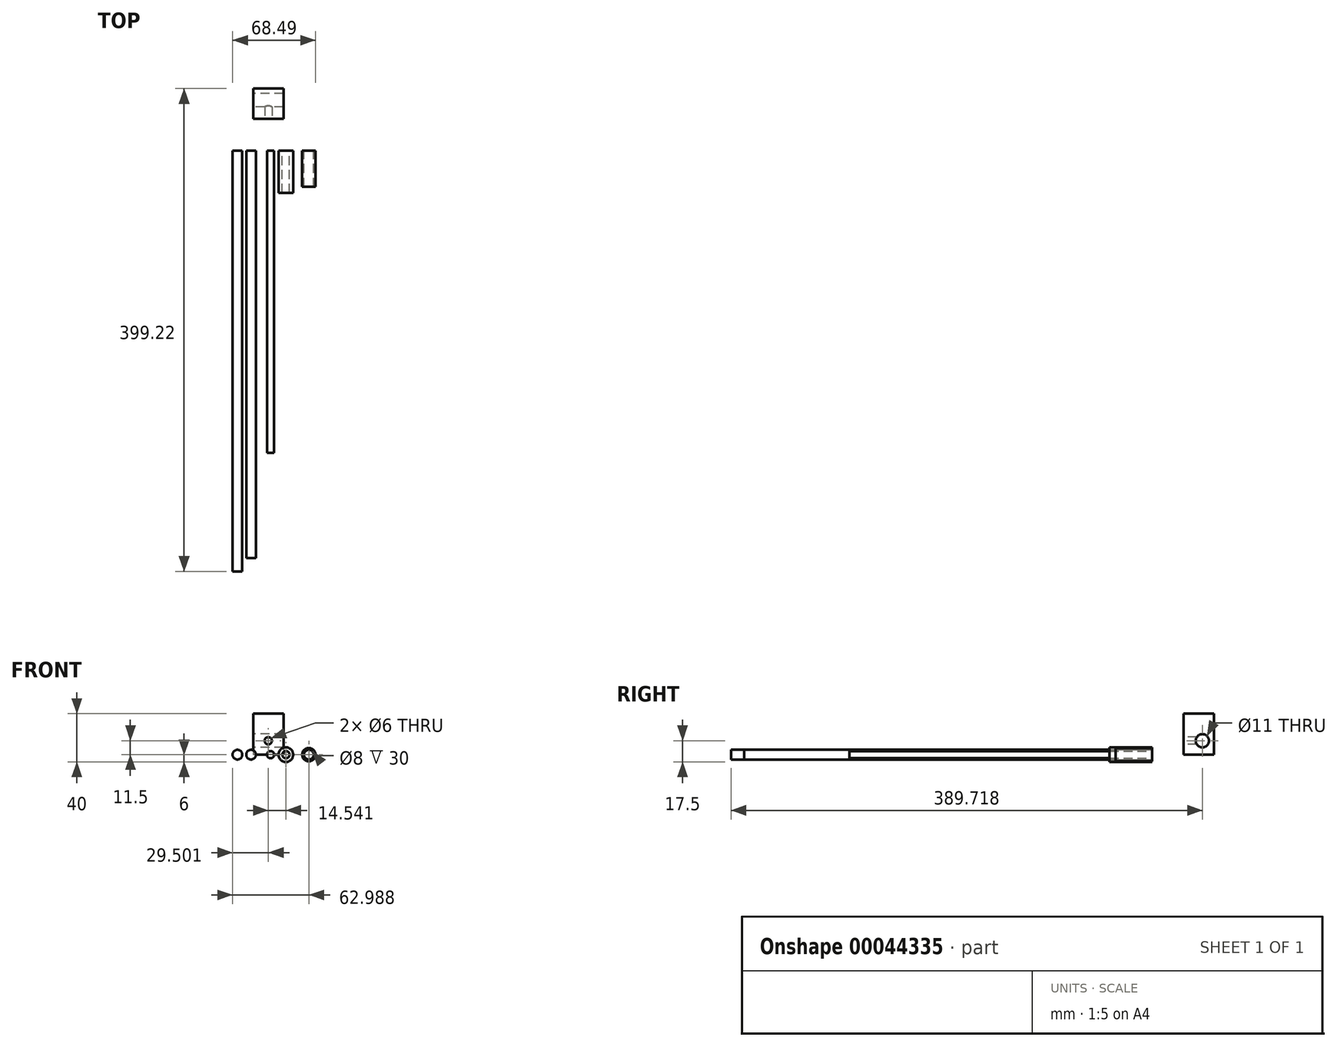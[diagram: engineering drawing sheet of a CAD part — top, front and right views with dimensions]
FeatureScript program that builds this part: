
annotation { "Feature Type Name" : "Feature", "Feature Type Description" : "" }
export const myFeature = defineFeature(function(context is Context, id is Id, definition is map)
    precondition{}
    {
        {
            var Q0;
            Q0=qCreatedBy(makeId("Front.planeOp"),FACE);
            var sketch = newSketch(context, id + "F0", { "sketchPlane" : qUnion([Q0])});
            skCircle(sketch, "E0", {"center": v(-61.9, 0) * mm, "radius": 4 * mm});
            skSolve(sketch);
        }
        {
            var Q0;
            Q0=makeQuery(id+"F0.imprint","IMPRINT",FACE,{"disambiguationData":[TD([[makeQuery(id+"F0.imprint","IMPRINT",EDGE,{"derivedFrom":sQuery(id+"F0.wireOp",EDGE,"E0")}),1.0]])]});
            extrude(context, id + "F1", {"entities" : qUnion([Q0]), "depth" : 348 * mm});
        }
        {
            var Q0;
            Q0=qCreatedBy(makeId("Front.planeOp"),FACE);
            var sketch = newSketch(context, id + "F2", { "sketchPlane" : qUnion([Q0])});
            skCircle(sketch, "E1", {"center": v(-45.77, 0) * mm, "radius": 3 * mm});
            skSolve(sketch);
        }
        {
            var Q0;
            Q0=makeQuery(id+"F2.imprint","IMPRINT",FACE,{"disambiguationData":[TD([[makeQuery(id+"F2.imprint","IMPRINT",EDGE,{"derivedFrom":sQuery(id+"F2.wireOp",EDGE,"E1")}),1.0]])]});
            extrude(context, id + "F3", {"entities" : qUnion([Q0]), "depth" : 250 * mm});
        }
        {
            var Q0;
            Q0=qCreatedBy(makeId("Front.planeOp"),FACE);
            var sketch = newSketch(context, id + "F4", { "sketchPlane" : qUnion([Q0])});
            skCircle(sketch, "E2", {"center": v(-33.08, 0) * mm, "radius": 3 * mm});
            skCircle(sketch, "E3", {"center": v(-33.08, 0) * mm, "radius": 6 * mm});
            skSolve(sketch);
        }
        {
            var Q0;
            Q0=makeQuery(id+"F4.imprint","IMPRINT",FACE,{"disambiguationData":[TD([[makeQuery(id+"F4.imprint","IMPRINT",EDGE,{"derivedFrom":sQuery(id+"F4.wireOp",EDGE,"E2")}),-1.0]])]});
            extrude(context, id + "F5", {"entities" : qUnion([Q0]), "depth" : 35 * mm});
        }
        {
            var Q0;
            Q0=makeQuery(id+"F1.opExtrude","SWEPT_BODY",BODY,{"disambiguationData":[OSD([sQuery(id+"F0.wireOp",EDGE,"E0")])]});
            transform(context, id + "F6", {"entities" : qUnion([Q0]), "transformType" : TransformType.TRANSLATION_3D, "dx" : -11.23 * mm, "dy" : 0 * mm, "dz" : 0 * mm, "makeCopy" : false});
        }
        {
            var Q0;
            Q0=qSketchRegion(id+"F0",true);
            extrude(context, id + "F7", {"entities" : qUnion([Q0]), "depth" : 337 * mm});
        }
        {
            var Q0;
            Q0=qCreatedBy(makeId("Front.planeOp"),FACE);
            var sketch = newSketch(context, id + "F8", { "sketchPlane" : qUnion([Q0])});
            skCircle(sketch, "E4", {"center": v(-14.13, 0) * mm, "radius": 4 * mm});
            skCircle(sketch, "E5", {"center": v(-14.13, 0) * mm, "radius": 5.5 * mm});
            skSolve(sketch);
        }
        {
            var Q0;
            Q0=makeQuery(id+"F8.imprint","IMPRINT",FACE,{"disambiguationData":[TD([[makeQuery(id+"F8.imprint","IMPRINT",EDGE,{"derivedFrom":sQuery(id+"F8.wireOp",EDGE,"E4")}),-1.0]])]});
            extrude(context, id + "F9", {"entities" : qUnion([Q0]), "depth" : 30 * mm});
        }
        {
            var Q0;
            Q0=qCreatedBy(makeId("Top.planeOp"),FACE);
            var sketch = newSketch(context, id + "F10", { "sketchPlane" : qUnion([Q0])});
            skLineSegment(sketch, "E6.bottom", {"start": v(-35.12, 51.22) * mm, "end": v(-60.12, 51.22) * mm});
            skLineSegment(sketch, "E6.top", {"start": v(-35.12, 26.22) * mm, "end": v(-60.12, 26.22) * mm});
            skLineSegment(sketch, "E6.left", {"start": v(-35.12, 51.22) * mm, "end": v(-35.12, 26.22) * mm});
            skLineSegment(sketch, "E6.right", {"start": v(-60.12, 51.22) * mm, "end": v(-60.12, 26.22) * mm});
            skSolve(sketch);
        }
        {
            var Q0;
            Q0=makeQuery(id+"F10.imprint","IMPRINT",FACE,{"disambiguationData":[TD([[makeQuery(id+"F10.imprint","IMPRINT",EDGE,{"derivedFrom":sQuery(id+"F10.wireOp",EDGE,"E6.bottom")}),1.0]])]});
            extrude(context, id + "F11", {"entities" : qUnion([Q0]), "depth" : 34 * mm});
        }
        {
            var Q0;
            Q0=makeQuery(id+"F11.opExtrude","SWEPT_FACE",FACE,{"disambiguationData":[OSD([sQuery(id+"F10.wireOp",EDGE,"E6.right")])]});
            var sketch = newSketch(context, id + "F12", { "sketchPlane" : qUnion([Q0])});
            skLineSegment(sketch, "E7", {"start": v(-32.12, 0) * mm, "end": v(-51.22, 0) * mm, "construction": true});
            skLineSegment(sketch, "E8", {"start": v(-51.22, 0) * mm, "end": v(-51.22, 22.36) * mm, "construction": true});
            skCircle(sketch, "E9", {"center": v(-41.72, 11.5) * mm, "radius": 5.5 * mm});
            skSolve(sketch);
        }
        {
            var Q0;
            Q0=makeQuery(id+"F12.imprint","IMPRINT",FACE,{"disambiguationData":[TD([[makeQuery(id+"F12.imprint","IMPRINT",EDGE,{"derivedFrom":sQuery(id+"F12.wireOp",EDGE,"E9")}),1.0]])]});
            extrude(context, id + "F13", {"entities" : qUnion([Q0]), "operationType" : NewBodyOperationType.REMOVE, "endBound" : BoundingType.THROUGH_ALL, "oppositeDirection" : true, "depth" : 25 * mm});
        }
        {
            var Q0;
            Q0=makeQuery(id+"F11.opExtrude","SWEPT_FACE",FACE,{"disambiguationData":[OSD([sQuery(id+"F10.wireOp",EDGE,"E6.top")])]});
            var sketch = newSketch(context, id + "F14", { "sketchPlane" : qUnion([Q0])});
            skLineSegment(sketch, "E10.0", {"start": v(-60.12, 6) * mm, "end": v(-60.12, 17) * mm, "construction": true});
            skLineSegment(sketch, "E11", {"start": v(-60.12, 17) * mm, "end": v(-35.12, 17) * mm, "construction": true});
            skLineSegment(sketch, "E12", {"start": v(-60.12, 6) * mm, "end": v(-35.12, 6) * mm, "construction": true});
            skLineSegment(sketch, "E13", {"start": v(-60.12, 17) * mm, "end": v(-60.12, 11.5) * mm, "construction": true});
            skLineSegment(sketch, "E14", {"start": v(-60.12, 11.5) * mm, "end": v(-35.12, 11.5) * mm, "construction": true});
            skCircle(sketch, "E15", {"center": v(-47.62, 11.5) * mm, "radius": 3 * mm});
            skSolve(sketch);
        }
        {
            var Q0;
            Q0=makeQuery(id+"F14.imprint","IMPRINT",FACE,{"disambiguationData":[TD([[makeQuery(id+"F14.imprint","IMPRINT",EDGE,{"derivedFrom":sQuery(id+"F14.wireOp",EDGE,"E15")}),1.0]])]});
            extrude(context, id + "F15", {"entities" : qUnion([Q0]), "operationType" : NewBodyOperationType.REMOVE, "endBound" : BoundingType.UP_TO_NEXT, "oppositeDirection" : true, "depth" : 25 * mm});
        }
    });
